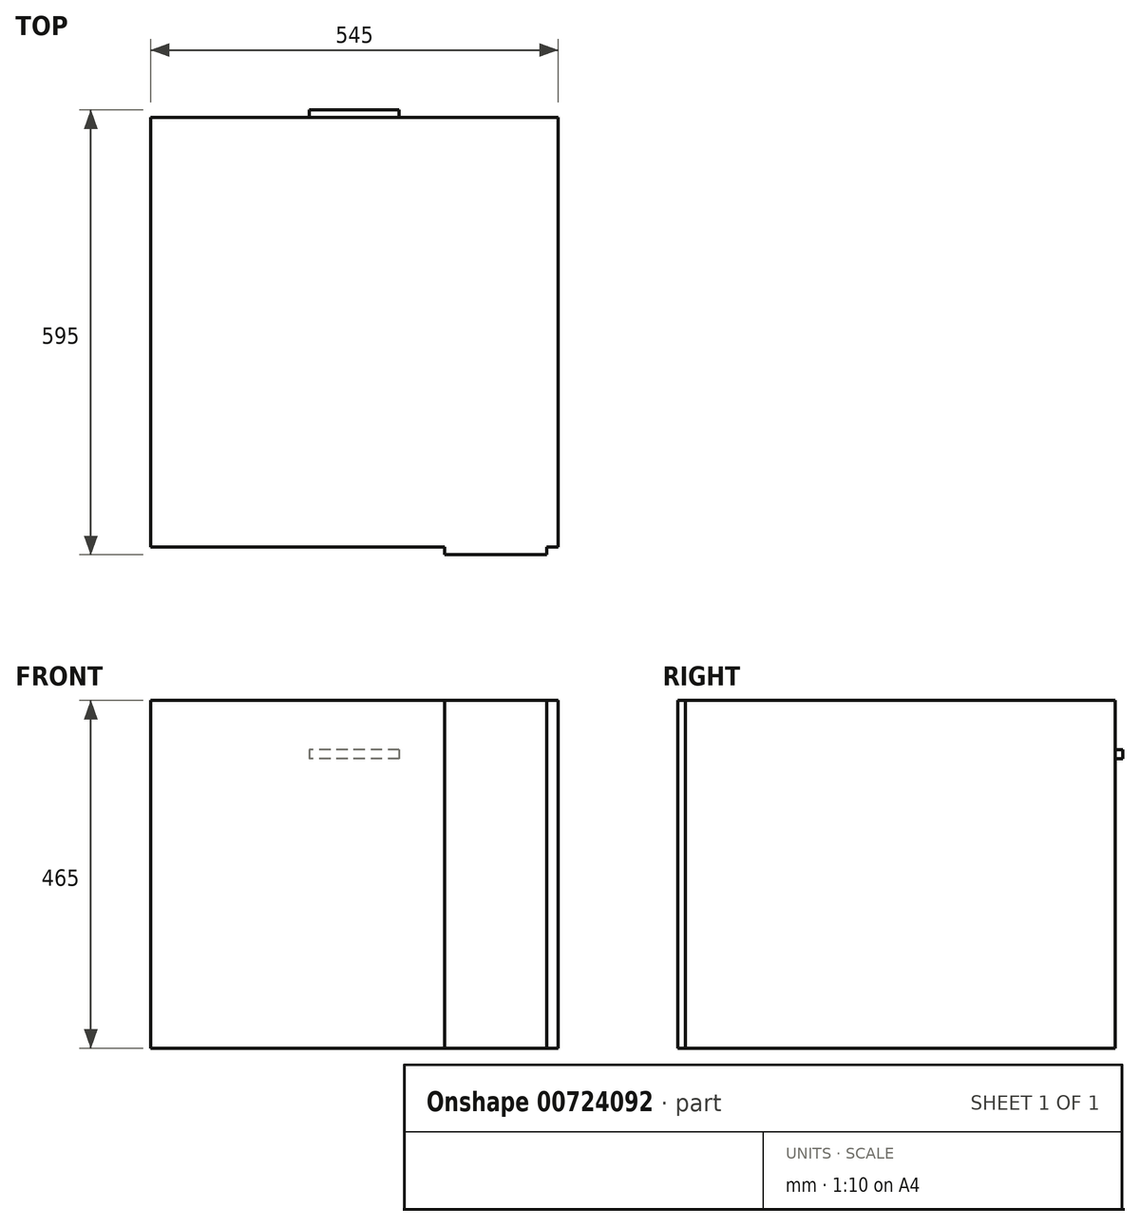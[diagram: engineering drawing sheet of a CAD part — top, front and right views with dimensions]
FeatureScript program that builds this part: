
annotation { "Feature Type Name" : "Feature", "Feature Type Description" : "" }
export const myFeature = defineFeature(function(context is Context, id is Id, definition is map)
    precondition{}
    {
        {
            var Q0;
            Q0=qCreatedBy(makeId("Front.planeOp"),FACE);
            var sketch = newSketch(context, id + "F0", { "sketchPlane" : qUnion([Q0])});
            skLineSegment(sketch, "E0.bottom", {"start": v(-272.5, 232.5) * mm, "end": v(272.5, 232.5) * mm});
            skLineSegment(sketch, "E0.top", {"start": v(-272.5, -232.5) * mm, "end": v(272.5, -232.5) * mm});
            skLineSegment(sketch, "E0.left", {"start": v(-272.5, 232.5) * mm, "end": v(-272.5, -232.5) * mm});
            skLineSegment(sketch, "E0.right", {"start": v(272.5, 232.5) * mm, "end": v(272.5, -232.5) * mm});
            skLineSegment(sketch, "E1", {"start": v(-272.5, 232.5) * mm, "end": v(272.5, -232.5) * mm, "construction": true});
            skSolve(sketch);
        }
        {
            var Q0;
            Q0=makeQuery(id+"F0.imprint","IMPRINT",FACE,{"disambiguationData":[TD([[makeQuery(id+"F0.imprint","IMPRINT",EDGE,{"derivedFrom":sQuery(id+"F0.wireOp",EDGE,"E0.bottom")}),-1.0]])]});
            extrude(context, id + "F1", {"entities" : qUnion([Q0]), "oppositeDirection" : true, "depth" : 575 * mm, "offsetDistance" : 25 * mm});
        }
        {
            var Q0;
            Q0=makeQuery(id+"F1.opExtrude","CAP_FACE",FACE,{"disambiguationData":[OSD([sQuery(id+"F0.wireOp",EDGE,"E0.bottom"),sQuery(id+"F0.wireOp",EDGE,"E0.top"),sQuery(id+"F0.wireOp",EDGE,"E0.left"),sQuery(id+"F0.wireOp",EDGE,"E0.right")])],"isStart":false});
            var sketch = newSketch(context, id + "F2", { "sketchPlane" : qUnion([Q0])});
            skLineSegment(sketch, "E2.bottom", {"start": v(-60, 166.4) * mm, "end": v(60, 166.4) * mm});
            skLineSegment(sketch, "E2.top", {"start": v(-60, 154.4) * mm, "end": v(60, 154.4) * mm});
            skLineSegment(sketch, "E2.left", {"start": v(-60, 166.4) * mm, "end": v(-60, 154.4) * mm});
            skLineSegment(sketch, "E2.right", {"start": v(60, 166.4) * mm, "end": v(60, 154.4) * mm});
            skLineSegment(sketch, "E3", {"start": v(0, 166.4) * mm, "end": v(0, 232.5) * mm, "construction": true});
            skSolve(sketch);
        }
        {
            var Q0;
            Q0=qSketchRegion(id+"F2",true);
            extrude(context, id + "F3", {"entities" : qUnion([Q0]), "operationType" : NewBodyOperationType.ADD, "depth" : 10 * mm, "offsetDistance" : 25 * mm});
        }
        {
            var Q0;
            Q0=makeQuery(id+"F1.opExtrude","CAP_FACE",FACE,{"disambiguationData":[OSD([sQuery(id+"F0.wireOp",EDGE,"E0.bottom"),sQuery(id+"F0.wireOp",EDGE,"E0.top"),sQuery(id+"F0.wireOp",EDGE,"E0.left"),sQuery(id+"F0.wireOp",EDGE,"E0.right")])],"isStart":true});
            var sketch = newSketch(context, id + "F4", { "sketchPlane" : qUnion([Q0])});
            skLineSegment(sketch, "E4.bottom", {"start": v(120.64, -232.5) * mm, "end": v(257, -232.5) * mm});
            skLineSegment(sketch, "E4.top", {"start": v(120.64, 232.5) * mm, "end": v(257, 232.5) * mm});
            skLineSegment(sketch, "E4.left", {"start": v(120.64, -232.5) * mm, "end": v(120.64, 232.5) * mm});
            skLineSegment(sketch, "E4.right", {"start": v(257, -232.5) * mm, "end": v(257, 232.5) * mm});
            skSolve(sketch);
        }
        {
            var Q0;
            Q0=qSketchRegion(id+"F4",true);
            extrude(context, id + "F5", {"entities" : qUnion([Q0]), "operationType" : NewBodyOperationType.ADD, "depth" : 10 * mm, "offsetDistance" : 25 * mm});
        }
    });
